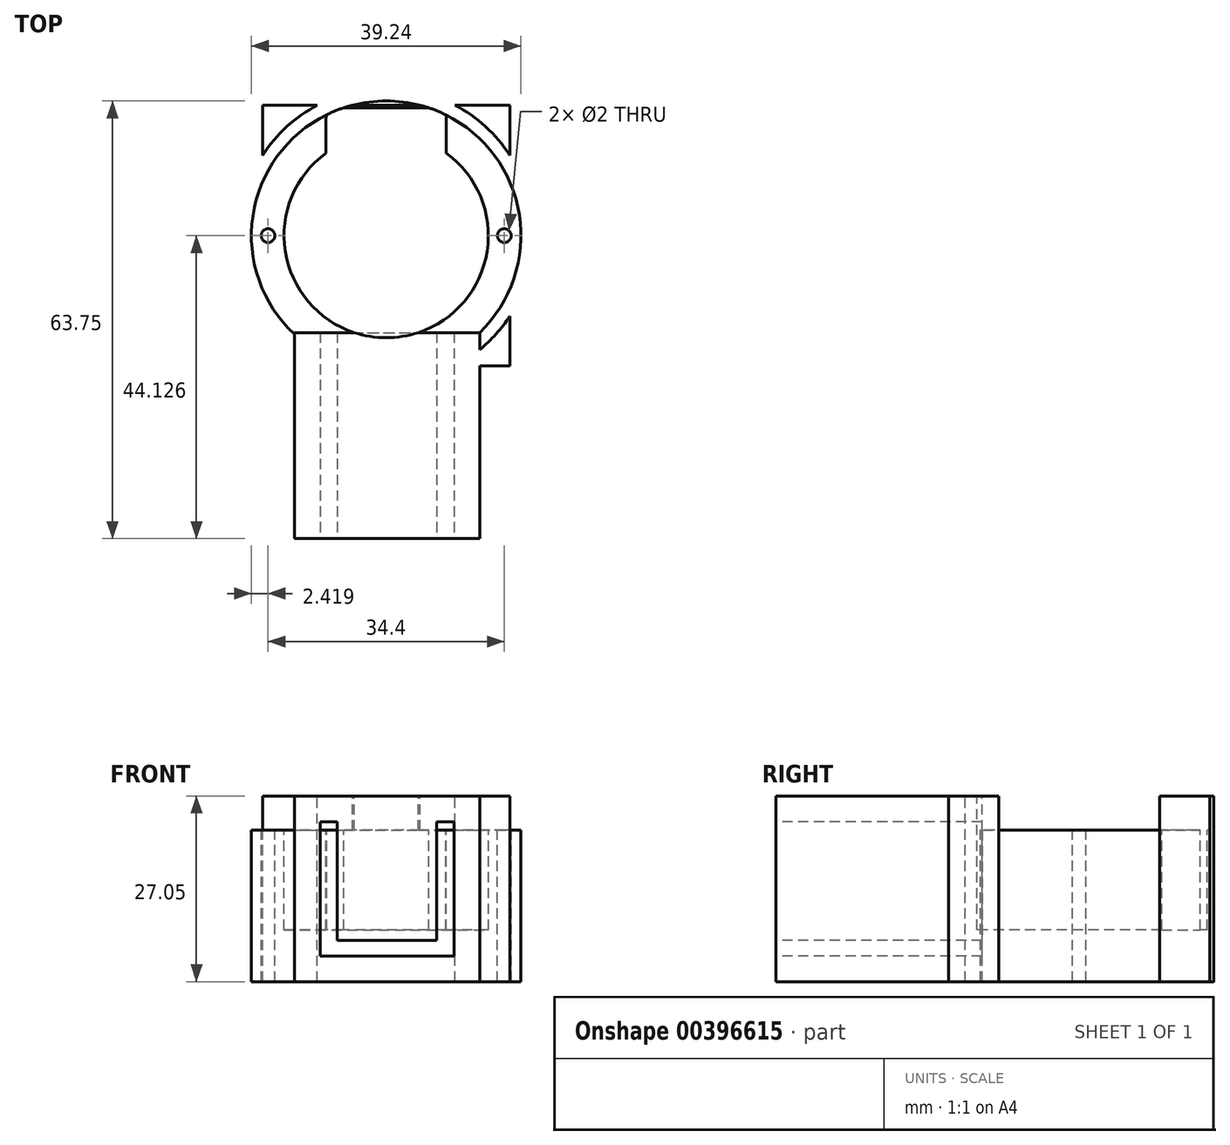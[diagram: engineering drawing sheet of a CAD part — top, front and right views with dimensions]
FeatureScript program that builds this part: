
annotation { "Feature Type Name" : "Feature", "Feature Type Description" : "" }
export const myFeature = defineFeature(function(context is Context, id is Id, definition is map)
    precondition{}
    {
        {
            var Q0;
            Q0=qCreatedBy(makeId("Front.planeOp"),FACE);
            var sketch = newSketch(context, id + "F0", { "sketchPlane" : qUnion([Q0])});
            skLineSegment(sketch, "E0", {"start": v(0, 65.65) * mm, "end": v(0, -40.44) * mm, "construction": true});
            skLineSegment(sketch, "E1", {"start": v(0, 0) * mm, "end": v(-9.75, 0) * mm});
            skLineSegment(sketch, "E2", {"start": v(-9.75, 0) * mm, "end": v(-9.75, 19.55) * mm});
            skLineSegment(sketch, "E3", {"start": v(-9.75, 19.55) * mm, "end": v(-7.25, 19.55) * mm});
            skLineSegment(sketch, "E4", {"start": v(-7.25, 19.55) * mm, "end": v(-7.25, 2.25) * mm});
            skLineSegment(sketch, "E5", {"start": v(-7.25, 2.25) * mm, "end": v(0, 2.25) * mm});
            skLineSegment(sketch, "E6.MirrorCS", {"start": v(9.75, 19.55) * mm, "end": v(7.25, 19.55) * mm});
            skLineSegment(sketch, "E7.MirrorCS", {"start": v(0, 0) * mm, "end": v(9.75, 0) * mm});
            skLineSegment(sketch, "E8.MirrorCS", {"start": v(9.75, 0) * mm, "end": v(9.75, 19.55) * mm});
            skLineSegment(sketch, "E9.MirrorCS", {"start": v(7.25, 19.55) * mm, "end": v(7.25, 2.25) * mm});
            skLineSegment(sketch, "E10.MirrorCS", {"start": v(7.25, 2.25) * mm, "end": v(0, 2.25) * mm});
            skLineSegment(sketch, "E11.0", {"start": v(-13.5, 23.3) * mm, "end": v(0, 23.3) * mm});
            skLineSegment(sketch, "E11.1", {"start": v(-13.5, -3.75) * mm, "end": v(-13.5, 23.3) * mm});
            skLineSegment(sketch, "E11.2", {"start": v(0, -3.75) * mm, "end": v(-13.5, -3.75) * mm});
            skLineSegment(sketch, "E12.MirrorCS", {"start": v(0, -3.75) * mm, "end": v(13.5, -3.75) * mm});
            skLineSegment(sketch, "E13.MirrorCS", {"start": v(13.5, 23.3) * mm, "end": v(0, 23.3) * mm});
            skLineSegment(sketch, "E14.MirrorCS", {"start": v(13.5, -3.75) * mm, "end": v(13.5, 23.3) * mm});
            skLineSegment(sketch, "E15", {"start": v(-13.5, 23.3) * mm, "end": v(-18, 23.3) * mm});
            skLineSegment(sketch, "E16", {"start": v(-18, 23.3) * mm, "end": v(-18, -3.75) * mm});
            skLineSegment(sketch, "E17", {"start": v(-18, -3.75) * mm, "end": v(-13.5, -3.75) * mm});
            skLineSegment(sketch, "E18.MirrorCS", {"start": v(18, -3.75) * mm, "end": v(13.5, -3.75) * mm});
            skLineSegment(sketch, "E19.MirrorCS", {"start": v(18, 23.3) * mm, "end": v(18, -3.75) * mm});
            skLineSegment(sketch, "E20.MirrorCS", {"start": v(13.5, 23.3) * mm, "end": v(18, 23.3) * mm});
            skSolve(sketch);
        }
        {
            var Q0;
            Q0=makeQuery(id+"F0.imprint","IMPRINT",FACE,{"disambiguationData":[TD([[makeQuery(id+"F0.imprint","IMPRINT",EDGE,{"derivedFrom":sQuery(id+"F0.wireOp",EDGE,"E1")}),1.0]])]});
            extrude(context, id + "F1", {"entities" : qUnion([Q0]), "oppositeDirection" : true, "depth" : 30 * mm});
        }
        {
            var Q0;
            {var subQ0=sQuery(id+"F0.wireOp",EDGE,"E13.MirrorCS");var subQ1=sQuery(id+"F0.wireOp",EDGE,"E11.0");Q0=makeQuery(id+"FVVeJcuvD0pZku6_1.boolean.opBoolean","MERGE",FACE,{"derivedFrom":[makeQuery(id+"F1.opExtrude","SWEPT_FACE",FACE,{"disambiguationData":[OSD([subQ1,subQ0])]}),makeQuery(id+"FVVeJcuvD0pZku6_1.opExtrude","SWEPT_FACE",FACE,{"disambiguationData":[OSD([subQ1,subQ0,sQuery(id+"F0.wireOp",EDGE,"E15"),sQuery(id+"F0.wireOp",EDGE,"E20.MirrorCS")])]})]});}
            var sketch = newSketch(context, id + "F2", { "sketchPlane" : qUnion([Q0])});
            skLineSegment(sketch, "E21.0", {"start": v(17.88, 25.13) * mm, "end": v(-0.12, 25.13) * mm});
            skLineSegment(sketch, "E21.1", {"start": v(17.88, 63.13) * mm, "end": v(17.88, 25.13) * mm});
            skLineSegment(sketch, "E21.2", {"start": v(17.88, 63.13) * mm, "end": v(-18.12, 63.13) * mm});
            skLineSegment(sketch, "E21.3", {"start": v(-18.12, 63.13) * mm, "end": v(-18.12, 25.13) * mm});
            skLineSegment(sketch, "E21.4", {"start": v(-0.12, 25.13) * mm, "end": v(-18.12, 25.13) * mm});
            skPoint(sketch, "E21.5", {"position": v(15.87, 25) * mm});
            skLineSegment(sketch, "E22", {"start": v(-0.12, 70.75) * mm, "end": v(-0.12, 19.83) * mm, "construction": true});
            skPoint(sketch, "E22.startSnap0", {"position": v(-0.12, 63.13) * mm});
            skPoint(sketch, "E23.orphan", {"position": v(-13.87, 25.13) * mm});
            skPoint(sketch, "E24.orphan", {"position": v(13.63, 25.13) * mm});
            skLineSegment(sketch, "E25", {"start": v(-27.37, 44.13) * mm, "end": v(23.52, 44.13) * mm, "construction": true});
            skPoint(sketch, "E25.startSnap0", {"position": v(-18.12, 44.13) * mm});
            skPoint(sketch, "E26", {"position": v(-0.12, 44.13) * mm});
            skCircle(sketch, "E27", {"center": v(-0.12, 44.13) * mm, "radius": 14.88 * mm});
            skCircle(sketch, "E28", {"center": v(-0.12, 44.13) * mm, "radius": 19.62 * mm});
            skPoint(sketch, "E29", {"position": v(17.08, 44.13) * mm});
            skCircle(sketch, "E30", {"center": v(17.08, 44.13) * mm, "radius": 1 * mm});
            skCircle(sketch, "E31.MirrorC", {"center": v(-17.32, 44.13) * mm, "radius": 1 * mm});
            skCircle(sketch, "E32", {"center": v(-0.12, 44.13) * mm, "radius": 21.48 * mm});
            skSolve(sketch);
        }
        {
            var Q0;
            {var subQ6=sQuery(id+"F2.wireOp",EDGE,"E28");var subQ14=sQuery(id+"F2.wireOp",EDGE,"E21.1");var subQ15=makeQuery(id+"F2.imprint","INTERSECT",VERTEX,{"disambiguationData":[OD(0.0)],"derivedFrom":[subQ14,subQ6]});Q0=makeQuery(id+"F2.imprint","IMPRINT",FACE,{"disambiguationData":[TD([[makeQuery(id+"F2.imprint","IMPRINT",EDGE,{"disambiguationData":[TD([[subQ15,-1.0]])],"derivedFrom":subQ14}),-1.0]])]});}
            var Q1;
            {var subQ0=sQuery(id+"F2.wireOp",EDGE,"E28");var subQ1=sQuery(id+"F2.wireOp",EDGE,"E21.3");var subQ2=makeQuery(id+"F2.imprint","INTERSECT",VERTEX,{"disambiguationData":[OD(0.0)],"derivedFrom":[subQ1,subQ0]});Q1=makeQuery(id+"F2.imprint","IMPRINT",FACE,{"disambiguationData":[TD([[makeQuery(id+"F2.imprint","IMPRINT",EDGE,{"disambiguationData":[TD([[subQ2,-1.0]])],"derivedFrom":subQ1}),-1.0]])]});}
            var Q2;
            {var subQ0=sQuery(id+"F2.wireOp",EDGE,"E28");var subQ1=sQuery(id+"F2.wireOp",EDGE,"E21.1");var subQ2=makeQuery(id+"F2.imprint","INTERSECT",VERTEX,{"disambiguationData":[OD(0.0)],"derivedFrom":[subQ1,subQ0]});Q2=makeQuery(id+"F2.imprint","IMPRINT",FACE,{"disambiguationData":[TD([[makeQuery(id+"F2.imprint","IMPRINT",EDGE,{"disambiguationData":[TD([[subQ2,-1.0]])],"derivedFrom":subQ1}),1.0]])]});}
            var Q3;
            {var subQ0=sQuery(id+"F2.wireOp",EDGE,"E27");var subQ1=makeQuery(id+"F1.opExtrude","CAP_EDGE",EDGE,{"disambiguationData":[OSD([sQuery(id+"F0.wireOp",EDGE,"E11.0"),sQuery(id+"F0.wireOp",EDGE,"E13.MirrorCS")])],"isStart":false});var subQ2=makeQuery(id+"F2.imprint","INTERSECT",VERTEX,{"disambiguationData":[OD(0.0)],"derivedFrom":[subQ1,subQ0]});Q3=makeQuery(id+"F2.imprint","IMPRINT",FACE,{"disambiguationData":[TD([[makeQuery(id+"F2.imprint","IMPRINT",EDGE,{"disambiguationData":[TD([[subQ2,1.0]])],"derivedFrom":subQ0}),1.0]])]});}
            var Q4;
            {var subQ0=sQuery(id+"F2.wireOp",EDGE,"E28");var subQ1=sQuery(id+"F2.wireOp",EDGE,"E21.2");var subQ2=makeQuery(id+"F2.imprint","INTERSECT",VERTEX,{"disambiguationData":[OD(0.0)],"derivedFrom":[subQ1,subQ0]});Q4=makeQuery(id+"F2.imprint","IMPRINT",FACE,{"disambiguationData":[TD([[makeQuery(id+"F2.imprint","IMPRINT",EDGE,{"disambiguationData":[TD([[subQ2,-1.0]])],"derivedFrom":subQ1}),-1.0]])]});}
            var Q5;
            {var subQ0=sQuery(id+"F2.wireOp",EDGE,"E31.MirrorC");var subQ1=sQuery(id+"F2.wireOp",EDGE,"E21.3");var subQ2=makeQuery(id+"F2.imprint","INTERSECT",VERTEX,{"disambiguationData":[OD(0.0)],"derivedFrom":[subQ1,subQ0]});Q5=makeQuery(id+"F2.imprint","IMPRINT",FACE,{"disambiguationData":[TD([[makeQuery(id+"F2.imprint","IMPRINT",EDGE,{"disambiguationData":[TD([[subQ2,-1.0]])],"derivedFrom":subQ1}),1.0]])]});}
            var Q6;
            {var subQ0=sQuery(id+"F2.wireOp",EDGE,"E31.MirrorC");var subQ1=sQuery(id+"F2.wireOp",EDGE,"E21.3");var subQ2=makeQuery(id+"F2.imprint","INTERSECT",VERTEX,{"disambiguationData":[OD(0.0)],"derivedFrom":[subQ1,subQ0]});Q6=makeQuery(id+"F2.imprint","IMPRINT",FACE,{"disambiguationData":[TD([[makeQuery(id+"F2.imprint","IMPRINT",EDGE,{"disambiguationData":[TD([[subQ2,-1.0]])],"derivedFrom":subQ1}),-1.0]])]});}
            var Q7;
            {var subQ0=sQuery(id+"F2.wireOp",EDGE,"E30");var subQ1=sQuery(id+"F2.wireOp",EDGE,"E21.1");var subQ2=makeQuery(id+"F2.imprint","INTERSECT",VERTEX,{"disambiguationData":[OD(0.0)],"derivedFrom":[subQ1,subQ0]});Q7=makeQuery(id+"F2.imprint","IMPRINT",FACE,{"disambiguationData":[TD([[makeQuery(id+"F2.imprint","IMPRINT",EDGE,{"disambiguationData":[TD([[subQ2,-1.0]])],"derivedFrom":subQ1}),-1.0]])]});}
            var Q8;
            {var subQ0=sQuery(id+"F2.wireOp",EDGE,"E30");var subQ1=sQuery(id+"F2.wireOp",EDGE,"E21.1");var subQ2=makeQuery(id+"F2.imprint","INTERSECT",VERTEX,{"disambiguationData":[OD(0.0)],"derivedFrom":[subQ1,subQ0]});Q8=makeQuery(id+"F2.imprint","IMPRINT",FACE,{"disambiguationData":[TD([[makeQuery(id+"F2.imprint","IMPRINT",EDGE,{"disambiguationData":[TD([[subQ2,-1.0]])],"derivedFrom":subQ1}),1.0]])]});}
            var Q9;
            {var subQ0=sQuery(id+"F2.wireOp",EDGE,"E32");var subQ1=sQuery(id+"F2.wireOp",EDGE,"E21.3");var subQ2=makeQuery(id+"F2.imprint","INTERSECT",VERTEX,{"disambiguationData":[OD(0.0)],"derivedFrom":[subQ1,subQ0]});Q9=makeQuery(id+"F2.imprint","IMPRINT",FACE,{"disambiguationData":[TD([[makeQuery(id+"F2.imprint","IMPRINT",EDGE,{"disambiguationData":[TD([[subQ2,-1.0]])],"derivedFrom":subQ1}),-1.0]])]});}
            var Q10;
            {var subQ0=sQuery(id+"F2.wireOp",EDGE,"E32");var subQ1=sQuery(id+"F2.wireOp",EDGE,"E21.2");var subQ2=makeQuery(id+"F2.imprint","INTERSECT",VERTEX,{"disambiguationData":[OD(1.0)],"derivedFrom":[subQ1,subQ0]});Q10=makeQuery(id+"F2.imprint","IMPRINT",FACE,{"disambiguationData":[TD([[makeQuery(id+"F2.imprint","IMPRINT",EDGE,{"disambiguationData":[TD([[subQ2,1.0]])],"derivedFrom":subQ1}),1.0]])]});}
            var Q11;
            {var subQ0=sQuery(id+"F2.wireOp",EDGE,"E32");var subQ1=sQuery(id+"F2.wireOp",EDGE,"E21.1");var subQ2=makeQuery(id+"F2.imprint","INTERSECT",VERTEX,{"disambiguationData":[OD(0.0)],"derivedFrom":[subQ1,subQ0]});Q11=makeQuery(id+"F2.imprint","IMPRINT",FACE,{"disambiguationData":[TD([[makeQuery(id+"F2.imprint","IMPRINT",EDGE,{"disambiguationData":[TD([[subQ2,-1.0]])],"derivedFrom":subQ1}),-1.0]])]});}
            var Q12;
            {var subQ0=sQuery(id+"F2.wireOp",EDGE,"E32");var subQ1=sQuery(id+"F2.wireOp",EDGE,"E21.2");var subQ2=makeQuery(id+"F2.imprint","INTERSECT",VERTEX,{"disambiguationData":[OD(0.0)],"derivedFrom":[subQ1,subQ0]});Q12=makeQuery(id+"F2.imprint","IMPRINT",FACE,{"disambiguationData":[TD([[makeQuery(id+"F2.imprint","IMPRINT",EDGE,{"disambiguationData":[TD([[subQ2,-1.0]])],"derivedFrom":subQ1}),-1.0]])]});}
            var Q13;
            {var subQ0=sQuery(id+"F2.wireOp",EDGE,"E32");var subQ1=sQuery(id+"F2.wireOp",EDGE,"E21.1");var subQ2=makeQuery(id+"F2.imprint","INTERSECT",VERTEX,{"disambiguationData":[OD(0.0)],"derivedFrom":[subQ1,subQ0]});Q13=makeQuery(id+"F2.imprint","IMPRINT",FACE,{"disambiguationData":[TD([[makeQuery(id+"F2.imprint","IMPRINT",EDGE,{"disambiguationData":[TD([[subQ2,-1.0]])],"derivedFrom":subQ1}),1.0]])]});}
            var Q14;
            {var subQ0=sQuery(id+"F2.wireOp",EDGE,"E32");var subQ1=sQuery(id+"F2.wireOp",EDGE,"E21.1");var subQ2=makeQuery(id+"F2.imprint","INTERSECT",VERTEX,{"disambiguationData":[OD(1.0)],"derivedFrom":[subQ1,subQ0]});Q14=makeQuery(id+"F2.imprint","IMPRINT",FACE,{"disambiguationData":[TD([[makeQuery(id+"F2.imprint","IMPRINT",EDGE,{"disambiguationData":[TD([[subQ2,1.0]])],"derivedFrom":subQ1}),-1.0]])]});}
            var Q15;
            {var subQ0=sQuery(id+"F2.wireOp",EDGE,"E32");var subQ1=sQuery(id+"F2.wireOp",EDGE,"E21.3");var subQ2=makeQuery(id+"F2.imprint","INTERSECT",VERTEX,{"disambiguationData":[OD(1.0)],"derivedFrom":[subQ1,subQ0]});Q15=makeQuery(id+"F2.imprint","IMPRINT",FACE,{"disambiguationData":[TD([[makeQuery(id+"F2.imprint","IMPRINT",EDGE,{"disambiguationData":[TD([[subQ2,1.0]])],"derivedFrom":subQ1}),1.0]])]});}
            var Q16;
            Q16=makeQuery(id+"F1.opExtrude","SWEPT_FACE",FACE,{"disambiguationData":[OSD([sQuery(id+"F0.wireOp",EDGE,"E11.2"),sQuery(id+"F0.wireOp",EDGE,"E12.MirrorCS")])]});
            extrude(context, id + "F3", {"entities" : qUnion([Q0, Q1, Q2, Q3, Q4, Q5, Q6, Q7, Q8, Q9, Q10, Q11, Q12, Q13, Q14, Q15]), "operationType" : NewBodyOperationType.ADD, "endBound" : BoundingType.UP_TO_SURFACE, "oppositeDirection" : true, "endBoundEntityFace" : qUnion([Q16]), "depth" : 25 * mm});
        }
        {
            var Q0;
            {var subQ0=sQuery(id+"F2.wireOp",EDGE,"E27");var subQ1=makeQuery(id+"F1.opExtrude","CAP_EDGE",EDGE,{"disambiguationData":[OSD([sQuery(id+"F0.wireOp",EDGE,"E11.0"),sQuery(id+"F0.wireOp",EDGE,"E13.MirrorCS")])],"isStart":false});var subQ2=makeQuery(id+"F2.imprint","INTERSECT",VERTEX,{"disambiguationData":[OD(0.0)],"derivedFrom":[subQ1,subQ0]});Q0=makeQuery(id+"F2.imprint","IMPRINT",FACE,{"disambiguationData":[TD([[makeQuery(id+"F2.imprint","IMPRINT",EDGE,{"disambiguationData":[TD([[subQ2,1.0]])],"derivedFrom":subQ0}),1.0]])]});}
            var Q1;
            {var subQ0=sQuery(id+"F2.wireOp",EDGE,"E27");var subQ1=makeQuery(id+"F1.opExtrude","CAP_EDGE",EDGE,{"disambiguationData":[OSD([sQuery(id+"F0.wireOp",EDGE,"E11.0"),sQuery(id+"F0.wireOp",EDGE,"E13.MirrorCS")])],"isStart":false});var subQ2=makeQuery(id+"F2.imprint","INTERSECT",VERTEX,{"disambiguationData":[OD(0.0)],"derivedFrom":[subQ1,subQ0]});Q1=makeQuery(id+"F2.imprint","IMPRINT",FACE,{"disambiguationData":[TD([[makeQuery(id+"F2.imprint","IMPRINT",EDGE,{"disambiguationData":[TD([[subQ2,-1.0]])],"derivedFrom":subQ0}),1.0]])]});}
            extrude(context, id + "F4", {"entities" : qUnion([Q0, Q1]), "operationType" : NewBodyOperationType.REMOVE, "oppositeDirection" : true, "depth" : 19.5 * mm});
        }
        {
            var Q0;
            {var subQ0=sQuery(id+"F2.wireOp",EDGE,"E31.MirrorC");var subQ1=sQuery(id+"F2.wireOp",EDGE,"E21.3");var subQ2=makeQuery(id+"F2.imprint","INTERSECT",VERTEX,{"disambiguationData":[OD(0.0)],"derivedFrom":[subQ1,subQ0]});Q0=makeQuery(id+"F2.imprint","IMPRINT",FACE,{"disambiguationData":[TD([[makeQuery(id+"F2.imprint","IMPRINT",EDGE,{"disambiguationData":[TD([[subQ2,-1.0]])],"derivedFrom":subQ1}),1.0]])]});}
            var Q1;
            {var subQ0=sQuery(id+"F2.wireOp",EDGE,"E31.MirrorC");var subQ1=sQuery(id+"F2.wireOp",EDGE,"E21.3");var subQ2=makeQuery(id+"F2.imprint","INTERSECT",VERTEX,{"disambiguationData":[OD(0.0)],"derivedFrom":[subQ1,subQ0]});Q1=makeQuery(id+"F2.imprint","IMPRINT",FACE,{"disambiguationData":[TD([[makeQuery(id+"F2.imprint","IMPRINT",EDGE,{"disambiguationData":[TD([[subQ2,-1.0]])],"derivedFrom":subQ1}),-1.0]])]});}
            var Q2;
            {var subQ0=sQuery(id+"F2.wireOp",EDGE,"E30");var subQ1=sQuery(id+"F2.wireOp",EDGE,"E21.1");var subQ2=makeQuery(id+"F2.imprint","INTERSECT",VERTEX,{"disambiguationData":[OD(0.0)],"derivedFrom":[subQ1,subQ0]});Q2=makeQuery(id+"F2.imprint","IMPRINT",FACE,{"disambiguationData":[TD([[makeQuery(id+"F2.imprint","IMPRINT",EDGE,{"disambiguationData":[TD([[subQ2,-1.0]])],"derivedFrom":subQ1}),-1.0]])]});}
            var Q3;
            {var subQ0=sQuery(id+"F2.wireOp",EDGE,"E30");var subQ1=sQuery(id+"F2.wireOp",EDGE,"E21.1");var subQ2=makeQuery(id+"F2.imprint","INTERSECT",VERTEX,{"disambiguationData":[OD(0.0)],"derivedFrom":[subQ1,subQ0]});Q3=makeQuery(id+"F2.imprint","IMPRINT",FACE,{"disambiguationData":[TD([[makeQuery(id+"F2.imprint","IMPRINT",EDGE,{"disambiguationData":[TD([[subQ2,-1.0]])],"derivedFrom":subQ1}),1.0]])]});}
            var Q4;
            Q4=sQuery(id+"F2.wireOp",EDGE,"E31.MirrorC");
            var Q5;
            Q5=sQuery(id+"F2.wireOp",EDGE,"E30");
            extrude(context, id + "F5", {"entities" : qUnion([Q0, Q1, Q2, Q3]), "operationType" : NewBodyOperationType.REMOVE, "surfaceEntities" : qUnion([Q4, Q5]), "oppositeDirection" : true, "depth" : 5 * mm});
        }
        {
            var Q0;
            {var subQ0=sQuery(id+"F0.wireOp",EDGE,"E13.MirrorCS");var subQ1=sQuery(id+"F0.wireOp",EDGE,"E11.0");Q0=makeQuery(id+"F3.boolean.opBoolean","MERGE",FACE,{"derivedFrom":[makeQuery(id+"F1.opExtrude","SWEPT_FACE",FACE,{"disambiguationData":[OSD([subQ1,subQ0])]}),makeQuery(id+"F3.opExtrude","CAP_FACE",FACE,{"disambiguationData":[OSD([subQ1,sQuery(id+"F0.wireOp",EDGE,"E11.1"),subQ0,sQuery(id+"F0.wireOp",EDGE,"E14.MirrorCS"),sQuery(id+"F0.wireOp",EDGE,"E15"),sQuery(id+"F0.wireOp",EDGE,"E20.MirrorCS"),sQuery(id+"F2.wireOp",EDGE,"E32")])],"isStart":true})]});}
            var sketch = newSketch(context, id + "F6", { "sketchPlane" : qUnion([Q0])});
            skArc(sketch, "E33.0", {"start": v(13.5, 27.51) * mm, "mid": v(-0.28, 65.6) * mm, "end": v(-13.5, 27.32) * mm});
            skLineSegment(sketch, "E34", {"start": v(-0.12, 29.25) * mm, "end": v(-0.12, 72.13) * mm, "construction": true});
            skPoint(sketch, "E35", {"position": v(-0.12, 62.75) * mm});
            skLineSegment(sketch, "E36", {"start": v(-0.12, 62.75) * mm, "end": v(-7.37, 62.75) * mm});
            skLineSegment(sketch, "E37", {"start": v(-8.87, 61.25) * mm, "end": v(-8.87, 56.15) * mm});
            skPoint(sketch, "E38.visualSharp", {"position": v(-8.87, 62.75) * mm});
            skArc(sketch, "E38.filletArc", {"start": v(-7.37, 62.75) * mm, "mid": v(-8.43, 62.31) * mm, "end": v(-8.87, 61.25) * mm});
            skArc(sketch, "E39", {"start": v(-8.87, 56.15) * mm, "mid": v(4.48, 29.98) * mm, "end": v(-0.12, 59) * mm});
            skArc(sketch, "E40", {"start": v(-0.12, 59) * mm, "mid": v(-4.72, 58.27) * mm, "end": v(-8.87, 56.15) * mm});
            skArc(sketch, "E41.MirrorCS", {"start": v(-0.12, 59) * mm, "mid": v(4.48, 58.27) * mm, "end": v(8.63, 56.15) * mm});
            skLineSegment(sketch, "E42.MirrorCS", {"start": v(-0.12, 62.75) * mm, "end": v(7.13, 62.75) * mm});
            skLineSegment(sketch, "E43.MirrorCS", {"start": v(8.63, 61.25) * mm, "end": v(8.63, 56.15) * mm});
            skArc(sketch, "E44.MirrorCS", {"start": v(7.13, 62.75) * mm, "mid": v(8.19, 62.31) * mm, "end": v(8.63, 61.25) * mm});
            skSolve(sketch);
        }
        {
            var Q0;
            Q0=makeQuery(id+"F6.imprint","IMPRINT",FACE,{"disambiguationData":[TD([[makeQuery(id+"F6.imprint","IMPRINT",EDGE,{"derivedFrom":sQuery(id+"F6.wireOp",EDGE,"E36")}),1.0]])]});
            var Q1;
            Q1=makeQuery(id+"F4.boolean.opBoolean","COPY",FACE,{"derivedFrom":makeQuery(id+"F4.opExtrude","CAP_FACE",FACE,{"disambiguationData":[OSD([sQuery(id+"F2.wireOp",EDGE,"E27")])],"isStart":false})});
            extrude(context, id + "F7", {"entities" : qUnion([Q0]), "operationType" : NewBodyOperationType.REMOVE, "endBound" : BoundingType.UP_TO_SURFACE, "oppositeDirection" : true, "endBoundEntityFace" : qUnion([Q1]), "depth" : 25 * mm});
        }
    });
